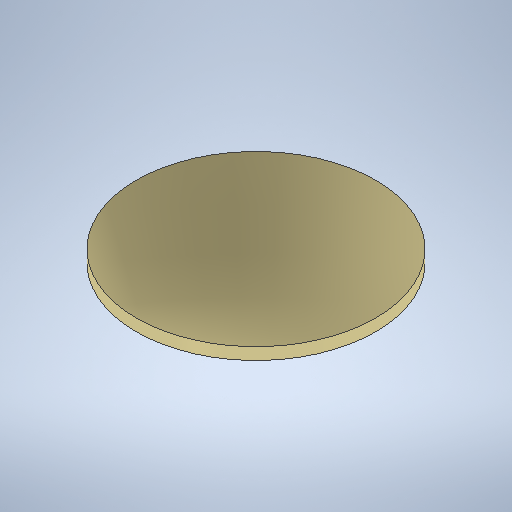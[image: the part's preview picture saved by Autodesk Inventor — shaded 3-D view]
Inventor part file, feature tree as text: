
AUTODESK INVENTOR PART (.ipt)
format: ipt  version: 2025.2 (Build 292293000, 293)  size: 233,472 bytes
history: native  units: in
note: dims shown in document units (in); Inventor stores cm internally (conversion verified against a paired STEP export)
features: extrude x1, sketch x1
ambient origin geometry x8: Origin, YZ Plane, XZ Plane, XY Plane, X Axis, Y Axis, Z Axis, Center Point
bodies: Solid1 (feature_tree)
feature tree (2):
  extrude  "Extrusion1"  Depth=0.0394in TaperAngle=0.0deg
  sketch  "Sketch1"  dims[d0=0.7874in d1=0.0394in d2=0.0in]
